# Revit family: agtatec_Record_SldngDrset_E-TSA-Telescopic_CurtainWallPanel
name_source: partatom
category: Curtain Panels
revit_build: Autodesk Revit Architecture 2015 (Build: 20140606_1530(x64)
units: mm (PartAtom-declared; Revit-internal decimal feet)

## types (12) — shared parameters
AccessoryOptions = Contact manufacturer
AcousticRating = None
AlternativeDoorsetGlazing = Part of glazing spec
AntiFingerTrapRequirement = Yes
Assembly Code = B2030110
BIMObjectName = agtatec_Record_SlidingDoorset_E-TSA-Telescopic_CurtainWallPanel
ClearHeightOfPassage = 2187 mm  [stored 7.1752 ft]
ClearanceZones = No
Colour = Customer specific
Configuration = 1 or 2
Construction Type = Automatic Sliding Door
Description = Automatic Sliding Door
Door Opening 2 = 600 mm
DoorIncluded = Yes
DoorSeal = yes
DoorsetFasteners = Screws
DoorsetOperation = Automatic
DriveUnit = agtatec_Record_Sliding Door, Sheet Metal (Painted Steel)
DurationUnit = year
ElectronicLock = Yes
Finish = Powder coated, Anodized, customer specific
FireExit = No
FireRating = None
FloorGuide = agtatec_Record_Sliding Door, Stainless Steel
FrameMaterial = Aluminium
FrameProfile = Aluminium
FrameSeal = Yes
GlassLayers = 2
GlassThickness1 = 6 mm (default)
GlassThickness2 = 6 mm (default)
GlassType = Part of glazing spec
GlazingAreaFraction = Depends on size. Can be calculated
HandicapAccessible = Yes
HasDrive = Yes
IfcExportAs = IfcDoorStyle
IfcExportType = Door
Inner Panel Width 1 = 632 mm
Inner Panel Width 2 = 620 mm
Interlancing Profile Height = 2195 mm  [stored 7.20144 ft]
IsExternal = Yes
LeafColourOptions = All RAL, customer specific
ManufacturerName = Record
ManufacturerURL = www.agta-record.com
Material = Aluminium
Model = record Telescopic Linear Slider
ModelReference = Depends on the configuration
NBSDescription = Sliding Doorset
NBSReference = 25-50-20/175
Name = SldngDrset_E-TSA-Telescopic_CurtainWallPanel_Record
OpeningWidth = 1200 mm
PanelFill = agtatec_Record_Sliding Door, Laminated Safety Glass (Clear)
PanelFrames = agtatec_Record_Sliding Door, Aluminium
PanelHeight = 2200 mm
PassageMountingProfile(OnlyApplicableForTypesWithTwoSidePanels) = No
ProductInformation = www.agta-record.com
ReferenceStandard = EN16005, EN16361, DIN 18650, etc.
ReplacementCost = Depends on the configuration and door type
SecurityRating = None
SelfClosing = Yes
ServiceLifeDuration = 10-15 years
Shape = Rectangular
Side Panel Width Left = 700 mm  [stored 2.29659 ft]
Side Panel Width Right = 700 mm  [stored 2.29659 ft]
SmokeStop = No
SupportLength = 1900 mm  [stored 6.2336 ft]
ThresholdRequired = Yes
ThresholdStripping = No additional required, part of the doorset
URL = www.agta-record.com
Uniclass2 = Ss_25_30_20_77
Version = Version 1.0
WallMountingProfile = Yes
WarrantyDescription = Depends on country
WarrantyDurationLabour = Depends on country
WarrantyDurationParts = Depends on country
WarrantyDurationUnit = Depends on country
WarrantyGuarantorLabour = Local door manufacturer
WarrantyGuarantorParts = Local door manufacturer
Weight = Depends on configuration and size
WithDriveCladding = Yes
WithinStandardSizes = Yes
WithoutDriveCladding(OnlyApplicableForTypesWithoutSidePanels) = No
zero-valued in all types: Cost, Door Opening 1, DoorOpening, DriveUnitExtraWidthLeft, DriveUnitExtraWidthRight, Extra Left, Extra Right, Extra Width Total, ExtraWidthLeft, ExtraWidthRight, NominalLength, ThermalTransmittance

## per-type parameters (varying)
| type | DriveUnitHeight | Interlacing profile left | Interlacing profile right | Left | Left Panel | Left Profile | NominalHeight | NominalWidth | Right | Right Panel | Right Profile | Support Length Left | Support Length Right | TotalHeight | TotalWidth | Without side panels |
| E-TSA-R 108 mm drive unit height - right - without side panel | 108 mm  [stored 0.354331 ft] | No | Yes | No | No | No | 2295 mm | 1299 mm  [stored 4.26181 ft] | Yes | No | No | 600 mm | 1300 mm  [stored 4.26509 ft] | 2295 mm | 1299 mm  [stored 4.26181 ft] | Yes |
| E-TSA-L 108 mm drive unit height - left - with side panel | 108 mm  [stored 0.354331 ft] | No | No | Yes | Yes | Yes | 2295 mm | 1955 mm  [stored 6.41404 ft] | No | No | No | 1300 mm  [stored 4.26509 ft] | 600 mm | 2295 mm | 1955 mm  [stored 6.41404 ft] | No |
| E-TSA-L 108 mm drive unit height - left - without side panel | 108 mm  [stored 0.354331 ft] | Yes | No | Yes | No | No | 2295 mm | 1299 mm  [stored 4.26181 ft] | No | No | No | 1300 mm  [stored 4.26509 ft] | 600 mm | 2295 mm | 1299 mm  [stored 4.26181 ft] | Yes |
| E-TSA-L 150 mm drive unit height - left - with side panel | 150 mm | No | No | Yes | Yes | Yes | 2337 mm  [stored 7.66732 ft] | 1955 mm  [stored 6.41404 ft] | No | No | No | 1300 mm  [stored 4.26509 ft] | 600 mm | 2337 mm  [stored 7.66732 ft] | 1955 mm  [stored 6.41404 ft] | No |
| E-TSA-L 150 mm drive unit height - left - without side panel | 150 mm | Yes | No | Yes | No | No | 2337 mm  [stored 7.66732 ft] | 1299 mm  [stored 4.26181 ft] | No | No | No | 1300 mm  [stored 4.26509 ft] | 600 mm | 2337 mm  [stored 7.66732 ft] | 1299 mm  [stored 4.26181 ft] | Yes |
| E-TSA-L 200 mm drive unit height - left - with side panel | 200 mm  [stored 0.656168 ft] | No | No | Yes | Yes | Yes | 2387 mm  [stored 7.83136 ft] | 1955 mm  [stored 6.41404 ft] | No | No | No | 1300 mm  [stored 4.26509 ft] | 600 mm | 2387 mm  [stored 7.83136 ft] | 1955 mm  [stored 6.41404 ft] | No |
| E-TSA-L 200 mm drive unit height - left - without side panel | 200 mm  [stored 0.656168 ft] | Yes | No | Yes | No | No | 2387 mm  [stored 7.83136 ft] | 1299 mm  [stored 4.26181 ft] | No | No | No | 1300 mm  [stored 4.26509 ft] | 600 mm | 2387 mm  [stored 7.83136 ft] | 1299 mm  [stored 4.26181 ft] | Yes |
| E-TSA-R 108 mm drive unit height - right - with side panel | 108 mm  [stored 0.354331 ft] | No | No | No | No | No | 2295 mm | 1955 mm  [stored 6.41404 ft] | Yes | Yes | Yes | 600 mm | 1300 mm  [stored 4.26509 ft] | 2295 mm | 1955 mm  [stored 6.41404 ft] | No |
| E-TSA-R 150 mm drive unit height - right - with side panel | 150 mm | No | No | No | No | No | 2337 mm  [stored 7.66732 ft] | 1955 mm  [stored 6.41404 ft] | Yes | Yes | Yes | 600 mm | 1300 mm  [stored 4.26509 ft] | 2337 mm  [stored 7.66732 ft] | 1955 mm  [stored 6.41404 ft] | No |
| E-TSA-R 150 mm drive unit height - right - without side panel | 150 mm | No | Yes | No | No | No | 2337 mm  [stored 7.66732 ft] | 1299 mm  [stored 4.26181 ft] | Yes | No | No | 600 mm | 1300 mm  [stored 4.26509 ft] | 2337 mm  [stored 7.66732 ft] | 1299 mm  [stored 4.26181 ft] | Yes |
| E-TSA-R 200 mm drive unit height - right - with side panel | 200 mm  [stored 0.656168 ft] | No | No | No | No | No | 2387 mm  [stored 7.83136 ft] | 1955 mm  [stored 6.41404 ft] | Yes | Yes | Yes | 600 mm | 1300 mm  [stored 4.26509 ft] | 2387 mm  [stored 7.83136 ft] | 1955 mm  [stored 6.41404 ft] | No |
| E-TSA-R 200 mm drive unit height - right - without side panel | 200 mm  [stored 0.656168 ft] | No | Yes | No | No | No | 2387 mm  [stored 7.83136 ft] | 1299 mm  [stored 4.26181 ft] | Yes | No | No | 600 mm | 1300 mm  [stored 4.26509 ft] | 2387 mm  [stored 7.83136 ft] | 1299 mm  [stored 4.26181 ft] | Yes |

note: [stored X ft] marks values corroborated as IEEE doubles in the binary element streams (Revit-internal decimal feet)

## geometry (parser evidence)
native form markers: Sweep x13
no freeform markers — native parametric forms only
